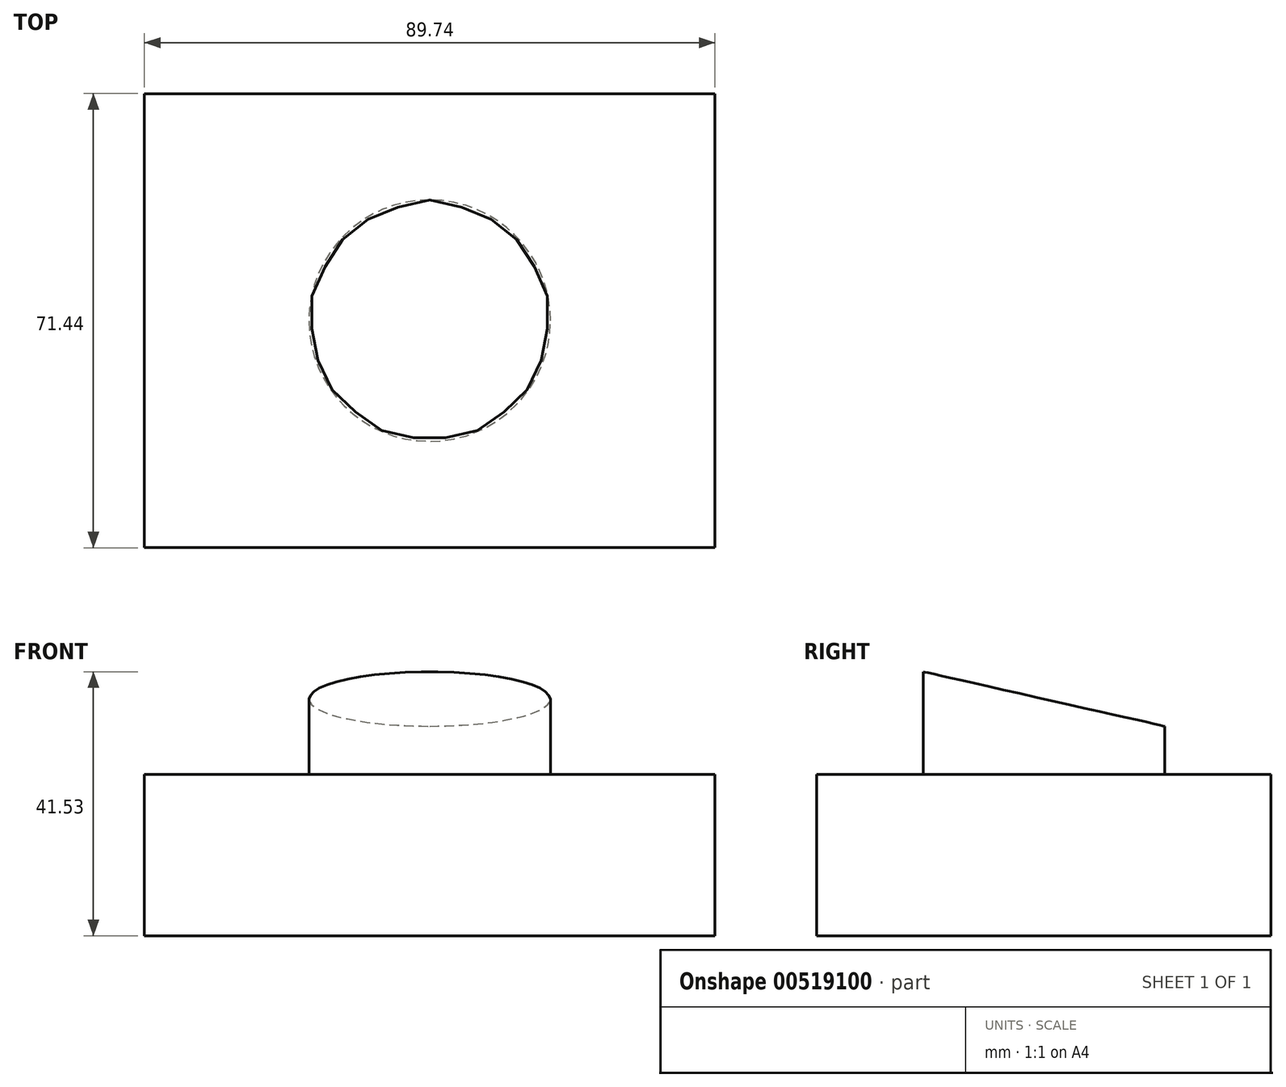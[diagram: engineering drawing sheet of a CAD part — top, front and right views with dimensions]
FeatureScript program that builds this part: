
annotation { "Feature Type Name" : "Feature", "Feature Type Description" : "" }
export const myFeature = defineFeature(function(context is Context, id is Id, definition is map)
    precondition{}
    {
        {
            var Q0;
            Q0=qCreatedBy(makeId("Top.planeOp"),FACE);
            var sketch = newSketch(context, id + "F0", { "sketchPlane" : qUnion([Q0])});
            skLineSegment(sketch, "E0.bottom", {"start": v(44.87, 35.72) * mm, "end": v(-44.87, 35.72) * mm});
            skLineSegment(sketch, "E0.top", {"start": v(44.87, -35.72) * mm, "end": v(-44.87, -35.72) * mm});
            skLineSegment(sketch, "E0.left", {"start": v(44.87, 35.72) * mm, "end": v(44.87, -35.72) * mm});
            skLineSegment(sketch, "E0.right", {"start": v(-44.87, 35.72) * mm, "end": v(-44.87, -35.72) * mm});
            skPoint(sketch, "E0.middle", {"position": v(0, 0) * mm});
            skSolve(sketch);
        }
        {
            var Q0;
            Q0 = qSketchRegion(id + "F0", true);
            extrude(context, id + "F1", {"entities" : qUnion([Q0]), "depth" : 25.4 * mm});
        }
        {
            var Q0;
            Q0=makeQuery(id+"F1.opExtrude","CAP_FACE",FACE,{"disambiguationData":[OSD([sQuery(id+"F0.wireOp",EDGE,"E0.bottom"),sQuery(id+"F0.wireOp",EDGE,"E0.top"),sQuery(id+"F0.wireOp",EDGE,"E0.left"),sQuery(id+"F0.wireOp",EDGE,"E0.right")])],"isStart":false});
            var sketch = newSketch(context, id + "F2", { "sketchPlane" : qUnion([Q0])});
            skCircle(sketch, "E1", {"center": v(0, 0) * mm, "radius": 18.99 * mm});
            skSolve(sketch);
        }
        {
            var Q0;
            Q0 = qSketchRegion(id + "F2", true);
            extrude(context, id + "F3", {"entities" : qUnion([Q0]), "operationType" : NewBodyOperationType.ADD, "depth" : 25.4 * mm});
        }
        {
            var Q0;
            Q0=qCreatedBy(makeId("Right.planeOp"),FACE);
            var sketch = newSketch(context, id + "F4", { "sketchPlane" : qUnion([Q0])});
            skLineSegment(sketch, "E2", {"start": v(-20.64, 41.9) * mm, "end": v(23.32, 31.98) * mm});
            skLineSegment(sketch, "E3", {"start": v(23.32, 31.98) * mm, "end": v(23.32, 53.96) * mm});
            skLineSegment(sketch, "E4", {"start": v(23.32, 53.96) * mm, "end": v(-20.64, 53.96) * mm});
            skLineSegment(sketch, "E5", {"start": v(-20.64, 53.96) * mm, "end": v(-20.64, 41.9) * mm});
            skSolve(sketch);
        }
        {
            var Q0;
            Q0 = qSketchRegion(id + "F4", true);
            extrude(context, id + "F5", {"entities" : qUnion([Q0]), "operationType" : NewBodyOperationType.REMOVE, "endBound" : BoundingType.SYMMETRIC, "oppositeDirection" : true, "depth" : 1270 * mm});
        }
    });
